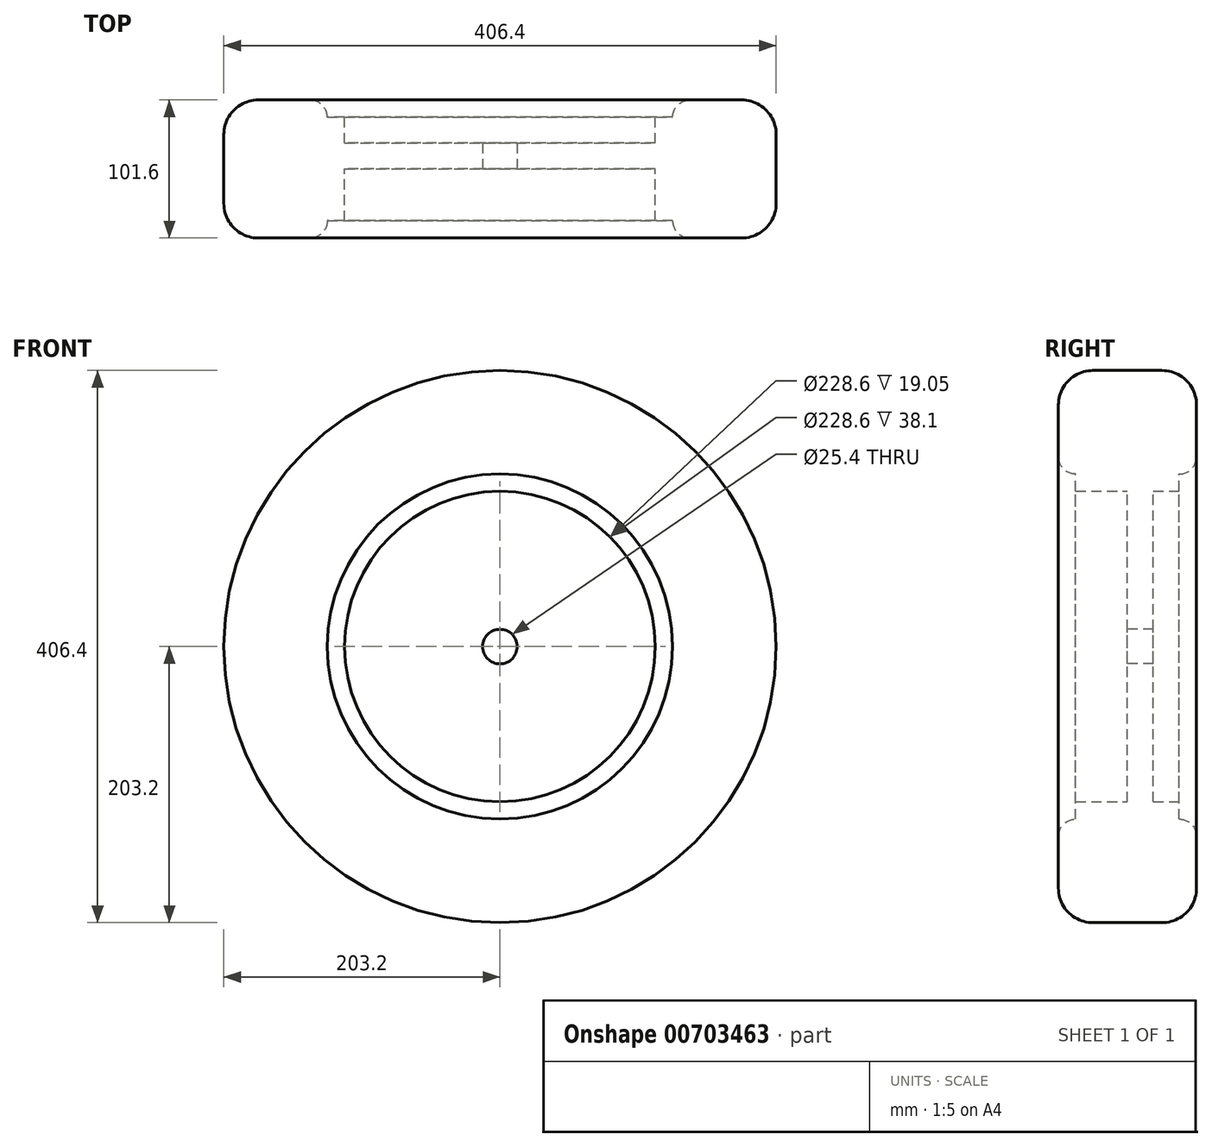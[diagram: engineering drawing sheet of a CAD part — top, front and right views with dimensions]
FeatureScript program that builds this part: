
annotation { "Feature Type Name" : "Feature", "Feature Type Description" : "" }
export const myFeature = defineFeature(function(context is Context, id is Id, definition is map)
    precondition{}
    {
        {
            var Q0;
            Q0=qCreatedBy(makeId("Front.planeOp"),FACE);
            var sketch = newSketch(context, id + "F0", { "sketchPlane" : qUnion([Q0])});
            skCircle(sketch, "E0", {"center": v(0, 0) * mm, "radius": 203.2 * mm});
            skCircle(sketch, "E1", {"center": v(0, 0) * mm, "radius": 127 * mm});
            skCircle(sketch, "E2", {"center": v(0, 0) * mm, "radius": 114.3 * mm});
            skCircle(sketch, "E3", {"center": v(0, 0) * mm, "radius": 12.7 * mm});
            skSolve(sketch);
        }
        {
            var Q0;
            Q0=makeQuery(id+"F0.imprint","IMPRINT",FACE,{"disambiguationData":[TD([[makeQuery(id+"F0.imprint","IMPRINT",EDGE,{"derivedFrom":sQuery(id+"F0.wireOp",EDGE,"E0")}),1.0]])]});
            extrude(context, id + "F1", {"entities" : qUnion([Q0]), "depth" : 50.8 * mm, "offsetDistance" : 25.4 * mm});
        }
        {
            var Q0;
            Q0=makeQuery(id+"F0.imprint","IMPRINT",FACE,{"disambiguationData":[TD([[makeQuery(id+"F0.imprint","IMPRINT",EDGE,{"derivedFrom":sQuery(id+"F0.wireOp",EDGE,"E0")}),1.0]])]});
            extrude(context, id + "F2", {"entities" : qUnion([Q0]), "operationType" : NewBodyOperationType.ADD, "oppositeDirection" : true, "depth" : 50.8 * mm, "offsetDistance" : 25.4 * mm});
        }
        {
            var Q0;
            Q0=makeQuery(id+"F0.imprint","IMPRINT",FACE,{"disambiguationData":[TD([[makeQuery(id+"F0.imprint","IMPRINT",EDGE,{"derivedFrom":sQuery(id+"F0.wireOp",EDGE,"E1")}),1.0]])]});
            extrude(context, id + "F3", {"entities" : qUnion([Q0]), "operationType" : NewBodyOperationType.ADD, "depth" : 38.1 * mm, "offsetDistance" : 25.4 * mm});
        }
        {
            var Q0;
            Q0=makeQuery(id+"F0.imprint","IMPRINT",FACE,{"disambiguationData":[TD([[makeQuery(id+"F0.imprint","IMPRINT",EDGE,{"derivedFrom":sQuery(id+"F0.wireOp",EDGE,"E1")}),1.0]])]});
            extrude(context, id + "F4", {"entities" : qUnion([Q0]), "operationType" : NewBodyOperationType.ADD, "oppositeDirection" : true, "depth" : 38.1 * mm, "offsetDistance" : 25.4 * mm});
        }
        {
            var Q0;
            Q0=makeQuery(id+"F1.opExtrude","CAP_EDGE",EDGE,{"disambiguationData":[OSD([sQuery(id+"F0.wireOp",EDGE,"E0")])],"isStart":false});
            var Q1;
            Q1=makeQuery(id+"F2.opExtrude","CAP_EDGE",EDGE,{"disambiguationData":[OSD([sQuery(id+"F0.wireOp",EDGE,"E0")])],"isStart":false});
            fillet(context, id + "F5", {"entities" : qUnion([Q0, Q1]), "radius" : 25.4 * mm, "tangentPropagation" : true, "allowEdgeOverflow" : false});
        }
        {
            var Q0;
            Q0=makeQuery(id+"F1.opExtrude","CAP_EDGE",EDGE,{"disambiguationData":[OSD([sQuery(id+"F0.wireOp",EDGE,"E1")])],"isStart":false});
            var Q1;
            Q1=makeQuery(id+"F2.opExtrude","CAP_EDGE",EDGE,{"disambiguationData":[OSD([sQuery(id+"F0.wireOp",EDGE,"E1")])],"isStart":false});
            fillet(context, id + "F6", {"entities" : qUnion([Q0, Q1]), "radius" : 12.7 * mm, "tangentPropagation" : true, "allowEdgeOverflow" : false});
        }
        {
            var Q0;
            Q0=makeQuery(id+"F0.imprint","IMPRINT",FACE,{"disambiguationData":[TD([[makeQuery(id+"F0.imprint","IMPRINT",EDGE,{"derivedFrom":sQuery(id+"F0.wireOp",EDGE,"E2")}),1.0]])]});
            extrude(context, id + "F7", {"entities" : qUnion([Q0]), "operationType" : NewBodyOperationType.ADD, "oppositeDirection" : true, "depth" : 19.05 * mm, "offsetDistance" : 25.4 * mm});
        }
    });
